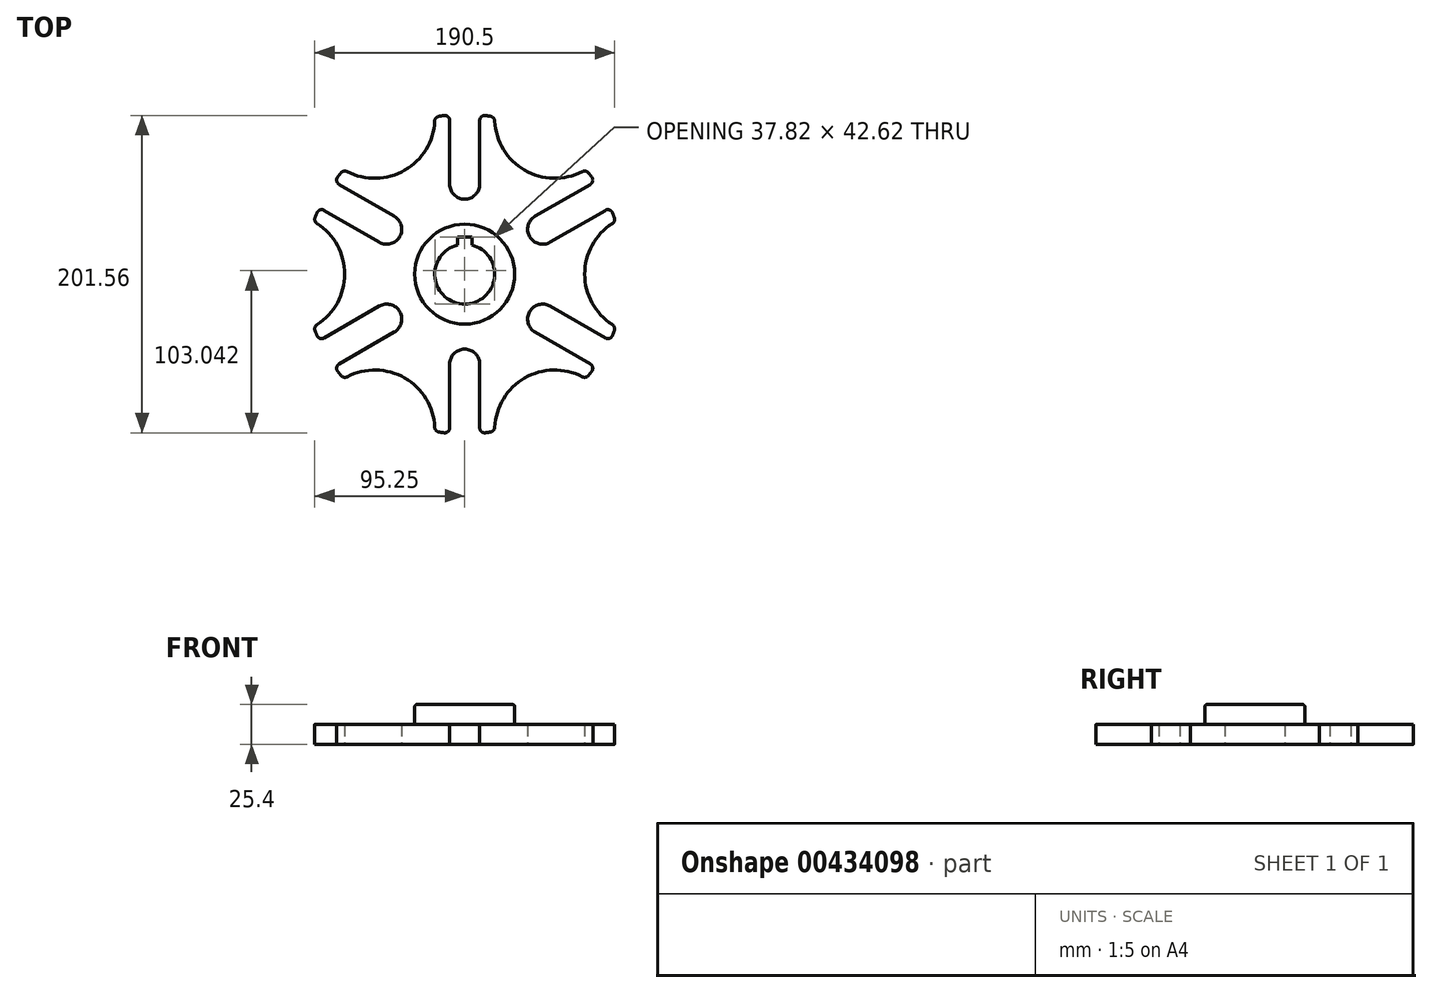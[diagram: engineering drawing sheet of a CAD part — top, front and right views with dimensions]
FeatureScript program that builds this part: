
annotation { "Feature Type Name" : "Feature", "Feature Type Description" : "" }
export const myFeature = defineFeature(function(context is Context, id is Id, definition is map)
    precondition{}
    {
        {
            var Q0;
            Q0=qCreatedBy(makeId("Top.planeOp"),FACE);
            var sketch = newSketch(context, id + "F0", { "sketchPlane" : qUnion([Q0])});
            skArc(sketch, "E0", {"start": v(-76.9, 66.4) * mm, "mid": v(-79.96, 62.68) * mm, "end": v(-82.84, 58.83) * mm});
            skArc(sketch, "E1", {"start": v(-9.53, 57.15) * mm, "mid": v(0, 47.63) * mm, "end": v(9.52, 57.15) * mm});
            skLineSegment(sketch, "E2", {"start": v(0, -101.6) * mm, "end": v(0, 101.6) * mm, "construction": true});
            skLineSegment(sketch, "E3.0", {"start": v(9.53, 57.15) * mm, "end": v(9.53, 101.6) * mm});
            skLineSegment(sketch, "E4.0", {"start": v(-9.52, 57.15) * mm, "end": v(-9.52, 101.6) * mm});
            skArc(sketch, "E5", {"start": v(-95.96, -33.4) * mm, "mid": v(-76.2, 0) * mm, "end": v(-95.96, 33.4) * mm});
            skLineSegment(sketch, "E6.1.0", {"start": v(-54.26, 20.33) * mm, "end": v(-92.75, 42.55) * mm});
            skLineSegment(sketch, "E6.1.1", {"start": v(-44.73, 36.82) * mm, "end": v(-83.23, 59.05) * mm});
            skArc(sketch, "E6.1.2", {"start": v(-54.26, 20.33) * mm, "mid": v(-41.24, 23.81) * mm, "end": v(-44.73, 36.82) * mm});
            skArc(sketch, "E6.1.3", {"start": v(-19.06, -99.8) * mm, "mid": v(-38.1, -66) * mm, "end": v(-76.9, -66.4) * mm});
            skLineSegment(sketch, "E6.2.0", {"start": v(-44.73, -36.82) * mm, "end": v(-83.23, -59.05) * mm});
            skLineSegment(sketch, "E6.2.1", {"start": v(-54.26, -20.33) * mm, "end": v(-92.75, -42.55) * mm});
            skArc(sketch, "E6.2.2", {"start": v(-44.73, -36.82) * mm, "mid": v(-41.24, -23.81) * mm, "end": v(-54.26, -20.33) * mm});
            skArc(sketch, "E6.2.3", {"start": v(76.9, -66.4) * mm, "mid": v(38.1, -66) * mm, "end": v(19.06, -99.8) * mm});
            skLineSegment(sketch, "E7.1.3.0", {"start": v(9.52, -57.15) * mm, "end": v(9.52, -101.6) * mm});
            skLineSegment(sketch, "E7.3.3.0", {"start": v(-9.53, -57.15) * mm, "end": v(-9.53, -101.6) * mm});
            skArc(sketch, "E7.6.3.0", {"start": v(9.52, -57.15) * mm, "mid": v(0, -47.63) * mm, "end": v(-9.53, -57.15) * mm});
            skArc(sketch, "E7.10.3.0", {"start": v(95.96, 33.4) * mm, "mid": v(76.2, 0) * mm, "end": v(95.96, -33.4) * mm});
            skLineSegment(sketch, "E7.1.4.0", {"start": v(54.26, -20.33) * mm, "end": v(92.75, -42.55) * mm});
            skLineSegment(sketch, "E7.3.4.0", {"start": v(44.73, -36.82) * mm, "end": v(83.23, -59.05) * mm});
            skArc(sketch, "E7.6.4.0", {"start": v(54.26, -20.33) * mm, "mid": v(41.24, -23.81) * mm, "end": v(44.73, -36.82) * mm});
            skArc(sketch, "E7.10.4.0", {"start": v(19.06, 99.8) * mm, "mid": v(38.1, 66) * mm, "end": v(76.9, 66.4) * mm});
            skLineSegment(sketch, "E7.1.5.0", {"start": v(44.73, 36.82) * mm, "end": v(83.23, 59.05) * mm});
            skLineSegment(sketch, "E7.3.5.0", {"start": v(54.26, 20.33) * mm, "end": v(92.75, 42.55) * mm});
            skArc(sketch, "E7.6.5.0", {"start": v(44.73, 36.82) * mm, "mid": v(41.24, 23.81) * mm, "end": v(54.26, 20.33) * mm});
            skArc(sketch, "E7.10.5.0", {"start": v(-76.9, 66.4) * mm, "mid": v(-38.1, 66) * mm, "end": v(-19.06, 99.8) * mm});
            skArc(sketch, "E8.trimOffspring", {"start": v(-92.36, 42.33) * mm, "mid": v(-94.27, 37.9) * mm, "end": v(-95.96, 33.4) * mm});
            skArc(sketch, "E9.trimOffspring", {"start": v(-95.96, -33.4) * mm, "mid": v(-94.27, -37.9) * mm, "end": v(-92.36, -42.33) * mm});
            skArc(sketch, "E10.trimOffspring", {"start": v(-9.53, 101.15) * mm, "mid": v(-14.3, 100.59) * mm, "end": v(-19.06, 99.8) * mm});
            skArc(sketch, "E11.trimOffspring", {"start": v(19.06, 99.8) * mm, "mid": v(14.3, 100.59) * mm, "end": v(9.53, 101.15) * mm});
            skArc(sketch, "E12.trimOffspring", {"start": v(82.84, 58.83) * mm, "mid": v(79.96, 62.68) * mm, "end": v(76.9, 66.4) * mm});
            skArc(sketch, "E13.trimOffspring", {"start": v(95.96, 33.4) * mm, "mid": v(94.27, 37.9) * mm, "end": v(92.36, 42.33) * mm});
            skArc(sketch, "E14.trimOffspring", {"start": v(92.36, -42.33) * mm, "mid": v(94.27, -37.9) * mm, "end": v(95.96, -33.4) * mm});
            skArc(sketch, "E15.trimOffspring", {"start": v(76.9, -66.4) * mm, "mid": v(79.96, -62.68) * mm, "end": v(82.84, -58.83) * mm});
            skArc(sketch, "E16.trimOffspring", {"start": v(9.52, -101.15) * mm, "mid": v(14.3, -100.59) * mm, "end": v(19.06, -99.8) * mm});
            skArc(sketch, "E17.trimOffspring", {"start": v(-19.06, -99.8) * mm, "mid": v(-14.3, -100.59) * mm, "end": v(-9.53, -101.15) * mm});
            skArc(sketch, "E18.trimOffspring", {"start": v(-82.84, -58.83) * mm, "mid": v(-79.96, -62.68) * mm, "end": v(-76.9, -66.4) * mm});
            skSolve(sketch);
        }
        {
            var Q0;
            {var subQ21=sQuery(id+"F0.wireOp",EDGE,"E0");Q0=makeQuery(id+"F0.imprint","IMPRINT",FACE,{"disambiguationData":[TD([[makeQuery(id+"F0.imprint","IMPRINT",EDGE,{"derivedFrom":subQ21}),1.0]])]});}
            extrude(context, id + "F1", {"entities" : qUnion([Q0]), "depth" : 12.7 * mm});
        }
        {
            var Q0;
            Q0=makeQuery(id+"F1.opExtrude","CAP_FACE",FACE,{"disambiguationData":[OSD([sQuery(id+"F0.wireOp",EDGE,"E0"),sQuery(id+"F0.wireOp",EDGE,"E1"),sQuery(id+"F0.wireOp",EDGE,"E3.0"),sQuery(id+"F0.wireOp",EDGE,"E4.0"),sQuery(id+"F0.wireOp",EDGE,"E5"),sQuery(id+"F0.wireOp",EDGE,"E6.1.0"),sQuery(id+"F0.wireOp",EDGE,"E6.1.1"),sQuery(id+"F0.wireOp",EDGE,"E6.1.2"),sQuery(id+"F0.wireOp",EDGE,"E6.1.3"),sQuery(id+"F0.wireOp",EDGE,"E6.2.0"),sQuery(id+"F0.wireOp",EDGE,"E6.2.1"),sQuery(id+"F0.wireOp",EDGE,"E6.2.2"),sQuery(id+"F0.wireOp",EDGE,"E6.2.3"),sQuery(id+"F0.wireOp",EDGE,"E7.1.3.0"),sQuery(id+"F0.wireOp",EDGE,"E7.3.3.0"),sQuery(id+"F0.wireOp",EDGE,"E7.6.3.0"),sQuery(id+"F0.wireOp",EDGE,"E7.10.3.0"),sQuery(id+"F0.wireOp",EDGE,"E7.1.4.0"),sQuery(id+"F0.wireOp",EDGE,"E7.3.4.0"),sQuery(id+"F0.wireOp",EDGE,"E7.6.4.0"),sQuery(id+"F0.wireOp",EDGE,"E7.10.4.0"),sQuery(id+"F0.wireOp",EDGE,"E7.1.5.0"),sQuery(id+"F0.wireOp",EDGE,"E7.3.5.0"),sQuery(id+"F0.wireOp",EDGE,"E7.6.5.0"),sQuery(id+"F0.wireOp",EDGE,"E7.10.5.0"),sQuery(id+"F0.wireOp",EDGE,"E8.trimOffspring"),sQuery(id+"F0.wireOp",EDGE,"E9.trimOffspring"),sQuery(id+"F0.wireOp",EDGE,"E10.trimOffspring"),sQuery(id+"F0.wireOp",EDGE,"E11.trimOffspring"),sQuery(id+"F0.wireOp",EDGE,"E12.trimOffspring"),sQuery(id+"F0.wireOp",EDGE,"E13.trimOffspring"),sQuery(id+"F0.wireOp",EDGE,"E14.trimOffspring"),sQuery(id+"F0.wireOp",EDGE,"E15.trimOffspring"),sQuery(id+"F0.wireOp",EDGE,"E16.trimOffspring"),sQuery(id+"F0.wireOp",EDGE,"E17.trimOffspring"),sQuery(id+"F0.wireOp",EDGE,"E18.trimOffspring")])],"isStart":false});
            var sketch = newSketch(context, id + "F2", { "sketchPlane" : qUnion([Q0])});
            skCircle(sketch, "E19", {"center": v(0, 0) * mm, "radius": 31.75 * mm});
            skSolve(sketch);
        }
        {
            var Q0;
            Q0=makeQuery(id+"F2.imprint","IMPRINT",FACE,{"disambiguationData":[TD([[makeQuery(id+"F2.imprint","IMPRINT",EDGE,{"derivedFrom":sQuery(id+"F2.wireOp",EDGE,"E19")}),1.0]])]});
            extrude(context, id + "F3", {"entities" : qUnion([Q0]), "operationType" : NewBodyOperationType.ADD, "depth" : 12.7 * mm});
        }
        {
            var Q0;
            Q0=makeQuery(id+"F3.opExtrude","CAP_FACE",FACE,{"disambiguationData":[OSD([sQuery(id+"F2.wireOp",EDGE,"E19")])],"isStart":false});
            var sketch = newSketch(context, id + "F4", { "sketchPlane" : qUnion([Q0])});
            skArc(sketch, "E20", {"start": v(-4.57, 18.5) * mm, "mid": v(0, -19.05) * mm, "end": v(4.57, 18.5) * mm});
            skLineSegment(sketch, "E21", {"start": v(0, 0) * mm, "end": v(0, 57.61) * mm, "construction": true});
            skLineSegment(sketch, "E22.0", {"start": v(4.57, 18.5) * mm, "end": v(4.57, 23.57) * mm});
            skLineSegment(sketch, "E23.0", {"start": v(-4.57, 18.5) * mm, "end": v(-4.57, 23.57) * mm});
            skLineSegment(sketch, "E24", {"start": v(-4.57, 23.57) * mm, "end": v(4.57, 23.57) * mm});
            skSolve(sketch);
        }
        {
            var Q0;
            Q0=makeQuery(id+"F4.imprint","IMPRINT",FACE,{"disambiguationData":[TD([[makeQuery(id+"F4.imprint","IMPRINT",EDGE,{"derivedFrom":sQuery(id+"F4.wireOp",EDGE,"E20")}),1.0]])]});
            extrude(context, id + "F5", {"entities" : qUnion([Q0]), "operationType" : NewBodyOperationType.REMOVE, "endBound" : BoundingType.THROUGH_ALL, "oppositeDirection" : true, "depth" : 25.4 * mm});
        }
        {
            var Q0;
            Q0=makeQuery(id+"F3.opExtrude","CAP_EDGE",EDGE,{"disambiguationData":[OSD([sQuery(id+"F2.wireOp",EDGE,"E19")])],"isStart":true});
            var Q1;
            Q1=makeQuery(id+"F3.opExtrude","CAP_EDGE",EDGE,{"disambiguationData":[OSD([sQuery(id+"F2.wireOp",EDGE,"E19")])],"isStart":false});
            fillet(context, id + "F6", {"entities" : qUnion([Q0, Q1]), "radius" : 1.59 * mm, "tangentPropagation" : true, "allowEdgeOverflow" : false});
        }
        {
            var Q0;
            Q0=makeQuery(id+"F1.opExtrude","SWEPT_EDGE",EDGE,{"disambiguationData":[OSD([sQuery(id+"F0.wireOp",EDGE,"E6.1.3"),sQuery(id+"F0.wireOp",EDGE,"E17.trimOffspring")])]});
            var Q1;
            Q1=makeQuery(id+"F1.opExtrude","SWEPT_EDGE",EDGE,{"disambiguationData":[OSD([sQuery(id+"F0.wireOp",EDGE,"E6.1.3"),sQuery(id+"F0.wireOp",EDGE,"E18.trimOffspring")])]});
            var Q2;
            Q2=makeQuery(id+"F1.opExtrude","SWEPT_EDGE",EDGE,{"disambiguationData":[OSD([sQuery(id+"F0.wireOp",EDGE,"E7.3.3.0"),sQuery(id+"F0.wireOp",EDGE,"E17.trimOffspring")])]});
            var Q3;
            Q3=makeQuery(id+"F1.opExtrude","SWEPT_EDGE",EDGE,{"disambiguationData":[OSD([sQuery(id+"F0.wireOp",EDGE,"E7.1.3.0"),sQuery(id+"F0.wireOp",EDGE,"E16.trimOffspring")])]});
            var Q4;
            Q4=makeQuery(id+"F1.opExtrude","SWEPT_EDGE",EDGE,{"disambiguationData":[OSD([sQuery(id+"F0.wireOp",EDGE,"E6.2.3"),sQuery(id+"F0.wireOp",EDGE,"E16.trimOffspring")])]});
            var Q5;
            Q5=makeQuery(id+"F1.opExtrude","SWEPT_EDGE",EDGE,{"disambiguationData":[OSD([sQuery(id+"F0.wireOp",EDGE,"E6.2.3"),sQuery(id+"F0.wireOp",EDGE,"E15.trimOffspring")])]});
            var Q6;
            Q6=makeQuery(id+"F1.opExtrude","SWEPT_EDGE",EDGE,{"disambiguationData":[OSD([sQuery(id+"F0.wireOp",EDGE,"E7.3.4.0"),sQuery(id+"F0.wireOp",EDGE,"E15.trimOffspring")])]});
            var Q7;
            Q7=makeQuery(id+"F1.opExtrude","SWEPT_EDGE",EDGE,{"disambiguationData":[OSD([sQuery(id+"F0.wireOp",EDGE,"E7.1.4.0"),sQuery(id+"F0.wireOp",EDGE,"E14.trimOffspring")])]});
            var Q8;
            Q8=makeQuery(id+"F1.opExtrude","SWEPT_EDGE",EDGE,{"disambiguationData":[OSD([sQuery(id+"F0.wireOp",EDGE,"E7.10.3.0"),sQuery(id+"F0.wireOp",EDGE,"E14.trimOffspring")])]});
            var Q9;
            Q9=makeQuery(id+"F1.opExtrude","SWEPT_EDGE",EDGE,{"disambiguationData":[OSD([sQuery(id+"F0.wireOp",EDGE,"E7.10.3.0"),sQuery(id+"F0.wireOp",EDGE,"E13.trimOffspring")])]});
            var Q10;
            Q10=makeQuery(id+"F1.opExtrude","SWEPT_EDGE",EDGE,{"disambiguationData":[OSD([sQuery(id+"F0.wireOp",EDGE,"E7.3.5.0"),sQuery(id+"F0.wireOp",EDGE,"E13.trimOffspring")])]});
            var Q11;
            Q11=makeQuery(id+"F1.opExtrude","SWEPT_EDGE",EDGE,{"disambiguationData":[OSD([sQuery(id+"F0.wireOp",EDGE,"E7.1.5.0"),sQuery(id+"F0.wireOp",EDGE,"E12.trimOffspring")])]});
            var Q12;
            Q12=makeQuery(id+"F1.opExtrude","SWEPT_EDGE",EDGE,{"disambiguationData":[OSD([sQuery(id+"F0.wireOp",EDGE,"E7.10.4.0"),sQuery(id+"F0.wireOp",EDGE,"E12.trimOffspring")])]});
            var Q13;
            Q13=makeQuery(id+"F1.opExtrude","SWEPT_EDGE",EDGE,{"disambiguationData":[OSD([sQuery(id+"F0.wireOp",EDGE,"E7.10.4.0"),sQuery(id+"F0.wireOp",EDGE,"E11.trimOffspring")])]});
            var Q14;
            Q14=makeQuery(id+"F1.opExtrude","SWEPT_EDGE",EDGE,{"disambiguationData":[OSD([sQuery(id+"F0.wireOp",EDGE,"E4.0"),sQuery(id+"F0.wireOp",EDGE,"E10.trimOffspring")])]});
            var Q15;
            Q15=makeQuery(id+"F1.opExtrude","SWEPT_EDGE",EDGE,{"disambiguationData":[OSD([sQuery(id+"F0.wireOp",EDGE,"E0"),sQuery(id+"F0.wireOp",EDGE,"E6.1.1")])]});
            var Q16;
            Q16=makeQuery(id+"F1.opExtrude","SWEPT_EDGE",EDGE,{"disambiguationData":[OSD([sQuery(id+"F0.wireOp",EDGE,"E5"),sQuery(id+"F0.wireOp",EDGE,"E8.trimOffspring")])]});
            var Q17;
            Q17=makeQuery(id+"F1.opExtrude","SWEPT_EDGE",EDGE,{"disambiguationData":[OSD([sQuery(id+"F0.wireOp",EDGE,"E6.2.1"),sQuery(id+"F0.wireOp",EDGE,"E9.trimOffspring")])]});
            var Q18;
            Q18=makeQuery(id+"F1.opExtrude","SWEPT_EDGE",EDGE,{"disambiguationData":[OSD([sQuery(id+"F0.wireOp",EDGE,"E3.0"),sQuery(id+"F0.wireOp",EDGE,"E11.trimOffspring")])]});
            var Q19;
            Q19=makeQuery(id+"F1.opExtrude","SWEPT_EDGE",EDGE,{"disambiguationData":[OSD([sQuery(id+"F0.wireOp",EDGE,"E7.10.5.0"),sQuery(id+"F0.wireOp",EDGE,"E10.trimOffspring")])]});
            var Q20;
            Q20=makeQuery(id+"F1.opExtrude","SWEPT_EDGE",EDGE,{"disambiguationData":[OSD([sQuery(id+"F0.wireOp",EDGE,"E0"),sQuery(id+"F0.wireOp",EDGE,"E7.10.5.0")])]});
            var Q21;
            Q21=makeQuery(id+"F1.opExtrude","SWEPT_EDGE",EDGE,{"disambiguationData":[OSD([sQuery(id+"F0.wireOp",EDGE,"E6.1.0"),sQuery(id+"F0.wireOp",EDGE,"E8.trimOffspring")])]});
            var Q22;
            Q22=makeQuery(id+"F1.opExtrude","SWEPT_EDGE",EDGE,{"disambiguationData":[OSD([sQuery(id+"F0.wireOp",EDGE,"E5"),sQuery(id+"F0.wireOp",EDGE,"E9.trimOffspring")])]});
            var Q23;
            Q23=makeQuery(id+"F1.opExtrude","SWEPT_EDGE",EDGE,{"disambiguationData":[OSD([sQuery(id+"F0.wireOp",EDGE,"E6.2.0"),sQuery(id+"F0.wireOp",EDGE,"E18.trimOffspring")])]});
            fillet(context, id + "F7", {"entities" : qUnion([Q0, Q1, Q2, Q3, Q4, Q5, Q6, Q7, Q8, Q9, Q10, Q11, Q12, Q13, Q14, Q15, Q16, Q17, Q18, Q19, Q20, Q21, Q22, Q23]), "radius" : 3.17 * mm, "tangentPropagation" : true, "allowEdgeOverflow" : false});
        }
    });
